# Revit family: 893302xx0--IN-TANK - Wall-hung toilet with integrated tank within the unit - Meridian - Roca - 893302xx0
name_source: partatom
category: Plumbing Fixtures
units: mm (PartAtom-declared; Revit-internal decimal feet)

## family parameters
Always vertical = Yes
Cut with Voids When Loaded = No
Host = Wall
OmniClass Number = 23.45.00.00
OmniClass Title = Sanitary, Laundry, and Cleaning Equipment
Part Type = Normal
Room Calculation Point = No
Round Connector Dimension = Use Diameter
Shared = No

## types (1)
- White - Meridian - Roca
    BIMobject category = WC
    Depth = 400.00
    Description = IN-TANK - Wall-hung toilet with integrated tank within the unit. Includes "I" type support, seat and cover. Needs power supply.
    Design country = Spain
    Edition number = 0
    Height = 400 mm  [stored 1.31234 ft]
    IFC Classification = Furnishing Element
    Inlet diameter = 40 mm  [stored 0.131234 ft]
    Installation instructions = http://www.roca.com
    Installation type = Wall-hung
    Length = 595 mm  [stored 1.9521 ft]
    Manufacturer name = Roca
    Manufacturer url = http://www.roca.com
    Material Main = White - Meridian - Roca
    Model = 893302..0
    NBS Reference Code = 35-65-90-97
    NBS Reference Description = Wc Systems
    Nominal height = 400.00
    Nominal width = 595.00
    Product SKU = A893302000
    Product data url = http://roca.bimobject.com
    Product family = Meridian|In-Tank
    Product group = Toilets
    QR code = https://www.roca.com
    Technical description = http://www.roca.com
    UNSPSC Code = 301815
    UNSPSC Name = Sanitary ware
    URL = http://www.roca.com
    Uniclass 1.4 Code = L7216
    Uniclass 1.4 Description = Toilets
    Uniclass 2.0 Code = SS-35-65-90-97
    Uniclass 2.0 Description = Wc Systems
    Waste water diameter = 102 mm  [stored 0.334646 ft]
    Weight Net (Kg) = 0
    Width = 400 mm  [stored 1.31234 ft]
    Youtube clip = http://www.youtube.com

note: [stored X ft] marks values corroborated as IEEE doubles in the binary element streams (Revit-internal decimal feet)

## geometry (parser evidence)
native form markers: Blend x2, Sweep x1
no freeform markers — native parametric forms only
